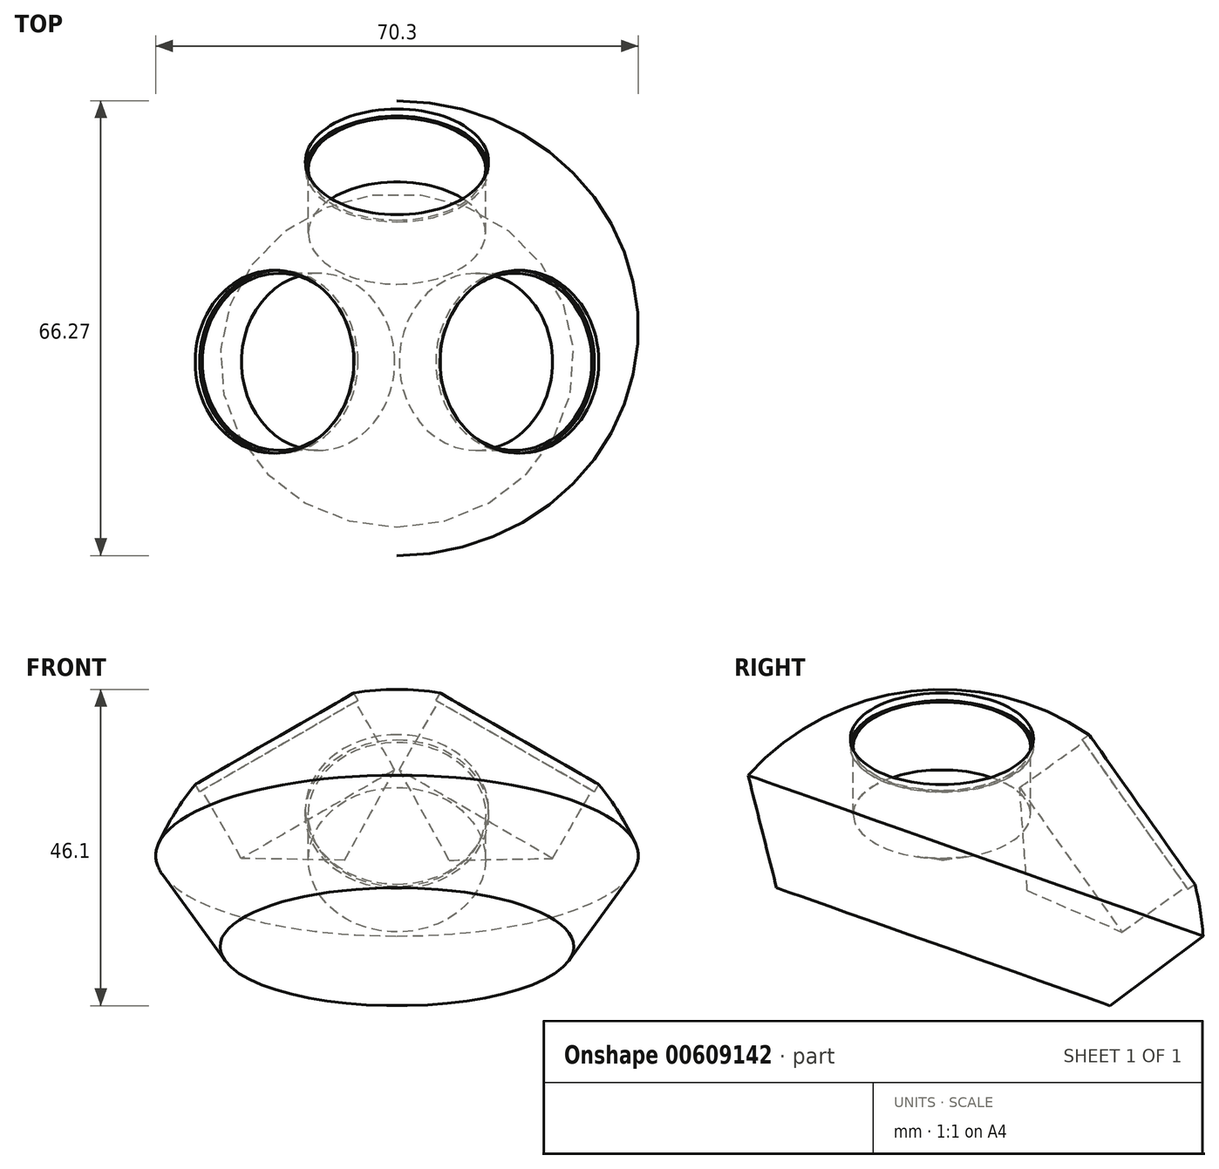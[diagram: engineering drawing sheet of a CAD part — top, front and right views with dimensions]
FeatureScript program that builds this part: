
annotation { "Feature Type Name" : "Feature", "Feature Type Description" : "" }
export const myFeature = defineFeature(function(context is Context, id is Id, definition is map)
    precondition{}
    {
        {
            var Q0;
            Q0=qCreatedBy(makeId("Front.planeOp"),FACE);
            var sketch = newSketch(context, id + "F0", { "sketchPlane" : qUnion([Q0])});
            skLineSegment(sketch, "E0", {"start": v(-38.1, 0) * mm, "end": v(38.1, 0) * mm});
            skArc(sketch, "E1", {"start": v(38.1, 0) * mm, "mid": v(0, 38.1) * mm, "end": v(-38.1, 0) * mm});
            skSolve(sketch);
        }
        {
            var Q0;
            Q0=makeQuery(id+"F0.imprint","IMPRINT",FACE,{"disambiguationData":[TD([[makeQuery(id+"F0.imprint","IMPRINT",EDGE,{"derivedFrom":sQuery(id+"F0.wireOp",EDGE,"E0")}),1.0]])]});
            var Q1;
            Q1=sQuery(id+"F0.wireOp",EDGE,"I0VPhN0o-a6IH-tLGe-MPig-f5kX4WHwjom2");
            var Q2;
            Q2=sQuery(id+"F0.wireOp",EDGE,"E0");
            revolve(context, id + "F1", {"entities" : qUnion([Q0]), "surfaceEntities" : qUnion([Q1]), "axis" : qUnion([Q2]), "revolveType" : RevolveType.FULL});
        }
        {
            var Q0;
            Q0=qCreatedBy(makeId("Front.planeOp"),FACE);
            var sketch = newSketch(context, id + "F2", { "sketchPlane" : qUnion([Q0])});
            skLineSegment(sketch, "E2", {"start": v(0, 0) * mm, "end": v(38.1, 66) * mm, "construction": true});
            skLineSegment(sketch, "E3", {"start": v(0, 0) * mm, "end": v(-38.1, 66) * mm, "construction": true});
            skSolve(sketch);
        }
        {
            var Q0;
            Q0=qCreatedBy(makeId("Right.planeOp"),FACE);
            var sketch = newSketch(context, id + "F3", { "sketchPlane" : qUnion([Q0])});
            skLineSegment(sketch, "E4", {"start": v(0, 0) * mm, "end": v(62.22, 43.99) * mm, "construction": true});
            skSolve(sketch);
        }
        {
            var Q0;
            Q0=sQuery(id+"F2.wireOp",VERTEX,"E3.end");
            var Q1;
            Q1=sQuery(id+"F2.wireOp",EDGE,"E3");
            cPlane(context, id + "F4", {"entities" : qUnion([Q0, Q1]), "cplaneType" : CPlaneType.LINE_POINT, "offset" : 25.4 * mm, "width" : 152.4 * mm, "height" : 152.4 * mm});
        }
        {
            var Q0;
            Q0=sQuery(id+"F2.wireOp",EDGE,"E2");
            var Q1;
            Q1=sQuery(id+"F2.wireOp",VERTEX,"E2.end");
            cPlane(context, id + "F5", {"entities" : qUnion([Q0, Q1]), "cplaneType" : CPlaneType.LINE_POINT, "offset" : 25.4 * mm, "width" : 152.4 * mm, "height" : 152.4 * mm});
        }
        {
            var Q0;
            Q0=sQuery(id+"F3.wireOp",EDGE,"E4");
            var Q1;
            Q1=sQuery(id+"F3.wireOp",VERTEX,"E4.end");
            cPlane(context, id + "F6", {"entities" : qUnion([Q0, Q1]), "cplaneType" : CPlaneType.LINE_POINT, "offset" : 25.4 * mm, "width" : 152.4 * mm, "height" : 152.4 * mm});
        }
        {
            var Q0;
            Q0=qCreatedBy(id+"F4.planeOp",FACE);
            var sketch = newSketch(context, id + "F7", { "sketchPlane" : qUnion([Q0])});
            skPoint(sketch, "E5", {"position": v(0, 0) * mm});
            skSolve(sketch);
        }
        {
            var Q0;
            Q0=qCreatedBy(id+"F5.planeOp",FACE);
            var sketch = newSketch(context, id + "F8", { "sketchPlane" : qUnion([Q0])});
            skPoint(sketch, "E6", {"position": v(0, 0) * mm});
            skSolve(sketch);
        }
        {
            var Q0;
            Q0=qCreatedBy(id+"F6.planeOp",FACE);
            var sketch = newSketch(context, id + "F9", { "sketchPlane" : qUnion([Q0])});
            skPoint(sketch, "E7", {"position": v(0, 0) * mm});
            skSolve(sketch);
        }
        {
            var Q0;
            Q0=sQuery(id+"F8.wireOp",VERTEX,"E6");
            var Q1;
            Q1=sQuery(id+"F7.wireOp",VERTEX,"E5");
            var Q2;
            Q2=sQuery(id+"F9.wireOp",VERTEX,"E7");
            var Q3;
            Q3=makeQuery(id+"F1.opRevolve","SWEPT_BODY",BODY,{"disambiguationData":[OSD([sQuery(id+"F0.wireOp",EDGE,"E0"),sQuery(id+"F0.wireOp",EDGE,"E1")])]});
            hole(context, id + "F10", {"style" : HoleStyle.C_BORE, "endStyle" : HoleEndStyle.BLIND, "holeDiameter" : 25.8 * mm, "cBoreDiameter" : 26.67 * mm, "cBoreDepth" : 1.27 * mm, "majorDiameter" : 6.35 * mm, "holeDepth" : 12.7 * mm, "isTappedThrough" : true, "tappedDepth" : 12.7 * mm, "tapClearance" : 3, "locations" : qUnion([Q0, Q1, Q2]), "scope" : qUnion([Q3])});
        }
        {
            var Q0;
            Q0=sQuery(id+"F3.wireOp",VERTEX,"E4.end");
            var Q1;
            Q1=sQuery(id+"F3.wireOp",VERTEX,"E4.start");
            var Q2;
            Q2=sQuery(id+"F2.wireOp",VERTEX,"E3.end");
            cPlane(context, id + "F11", {"entities" : qUnion([Q0, Q1, Q2]), "cplaneType" : CPlaneType.THREE_POINT, "offset" : 25.4 * mm, "width" : 152.4 * mm, "height" : 152.4 * mm});
        }
        {
            var Q0;
            Q0=sQuery(id+"F3.wireOp",EDGE,"E4");
            cPoint(context, id + "F12", {"entities" : qUnion([Q0]), "parameter" : 0.5});
        }
        {
            var Q0;
            Q0=sQuery(id+"F2.wireOp",EDGE,"E2");
            cPoint(context, id + "F13", {"entities" : qUnion([Q0]), "parameter" : 0.5});
        }
        {
            var Q0;
            Q0=sQuery(id+"F2.wireOp",EDGE,"E3");
            cPoint(context, id + "F14", {"entities" : qUnion([Q0]), "parameter" : 0.5});
        }
        {
            var Q0;
            Q0 = qCreatedBy(id + "F12" ,VERTEX);
            var Q1;
            Q1 = qCreatedBy(id + "F13" ,VERTEX);
            var Q2;
            Q2 = qCreatedBy(id + "F14" ,VERTEX);
            cPlane(context, id + "F15", {"entities" : qUnion([Q0, Q1, Q2]), "cplaneType" : CPlaneType.THREE_POINT, "offset" : 25.4 * mm, "width" : 152.4 * mm, "height" : 152.4 * mm});
        }
        {
            var Q0;
            Q0=qCreatedBy(id+"F15.planeOp",FACE);
            cPlane(context, id + "F16", {"entities" : qUnion([Q0]), "cplaneType" : CPlaneType.OFFSET, "offset" : 30.48 * mm, "oppositeDirection" : true, "width" : 152.4 * mm, "height" : 152.4 * mm});
        }
        {
            var Q0;
            Q0=qCreatedBy(id+"F16.planeOp",FACE);
            var sketch = newSketch(context, id + "F17", { "sketchPlane" : qUnion([Q0])});
            skLineSegment(sketch, "E8.bottom", {"start": v(48.78, -53.44) * mm, "end": v(-53.03, -53.44) * mm});
            skLineSegment(sketch, "E8.top", {"start": v(48.78, 63.78) * mm, "end": v(-53.03, 63.78) * mm});
            skLineSegment(sketch, "E8.left", {"start": v(48.78, -53.44) * mm, "end": v(48.78, 63.78) * mm});
            skLineSegment(sketch, "E8.right", {"start": v(-53.03, -53.44) * mm, "end": v(-53.03, 63.78) * mm});
            skSolve(sketch);
        }
        {
            var Q0;
            Q0=makeQuery(id+"F17.imprint","IMPRINT",FACE,{"disambiguationData":[TD([[makeQuery(id+"F17.imprint","IMPRINT",EDGE,{"derivedFrom":sQuery(id+"F17.wireOp",EDGE,"E8.bottom")}),-1.0]])]});
            extrude(context, id + "F18", {"entities" : qUnion([Q0]), "operationType" : NewBodyOperationType.REMOVE, "endBound" : BoundingType.THROUGH_ALL, "oppositeDirection" : true, "depth" : 25.4 * mm, "offsetDistance" : 25.4 * mm});
        }
        {
            var Q0;
            Q0=makeQuery(id+"F18.boolean.opBoolean","INTERSECT",EDGE,{"derivedFrom":[makeQuery(id+"F1.opRevolve","SWEPT_FACE",FACE,{"disambiguationData":[OSD([sQuery(id+"F0.wireOp",EDGE,"E1")])]}),makeQuery(id+"F18.opExtrude","CAP_FACE",FACE,{"disambiguationData":[OSD([sQuery(id+"F17.wireOp",EDGE,"E8.bottom"),sQuery(id+"F17.wireOp",EDGE,"E8.top"),sQuery(id+"F17.wireOp",EDGE,"E8.left"),sQuery(id+"F17.wireOp",EDGE,"E8.right")])],"isStart":true})]});
            chamfer(context, id + "F19", {"entities" : qUnion([Q0]), "width" : 10.16 * mm, "tangentPropagation" : true});
        }
    });
